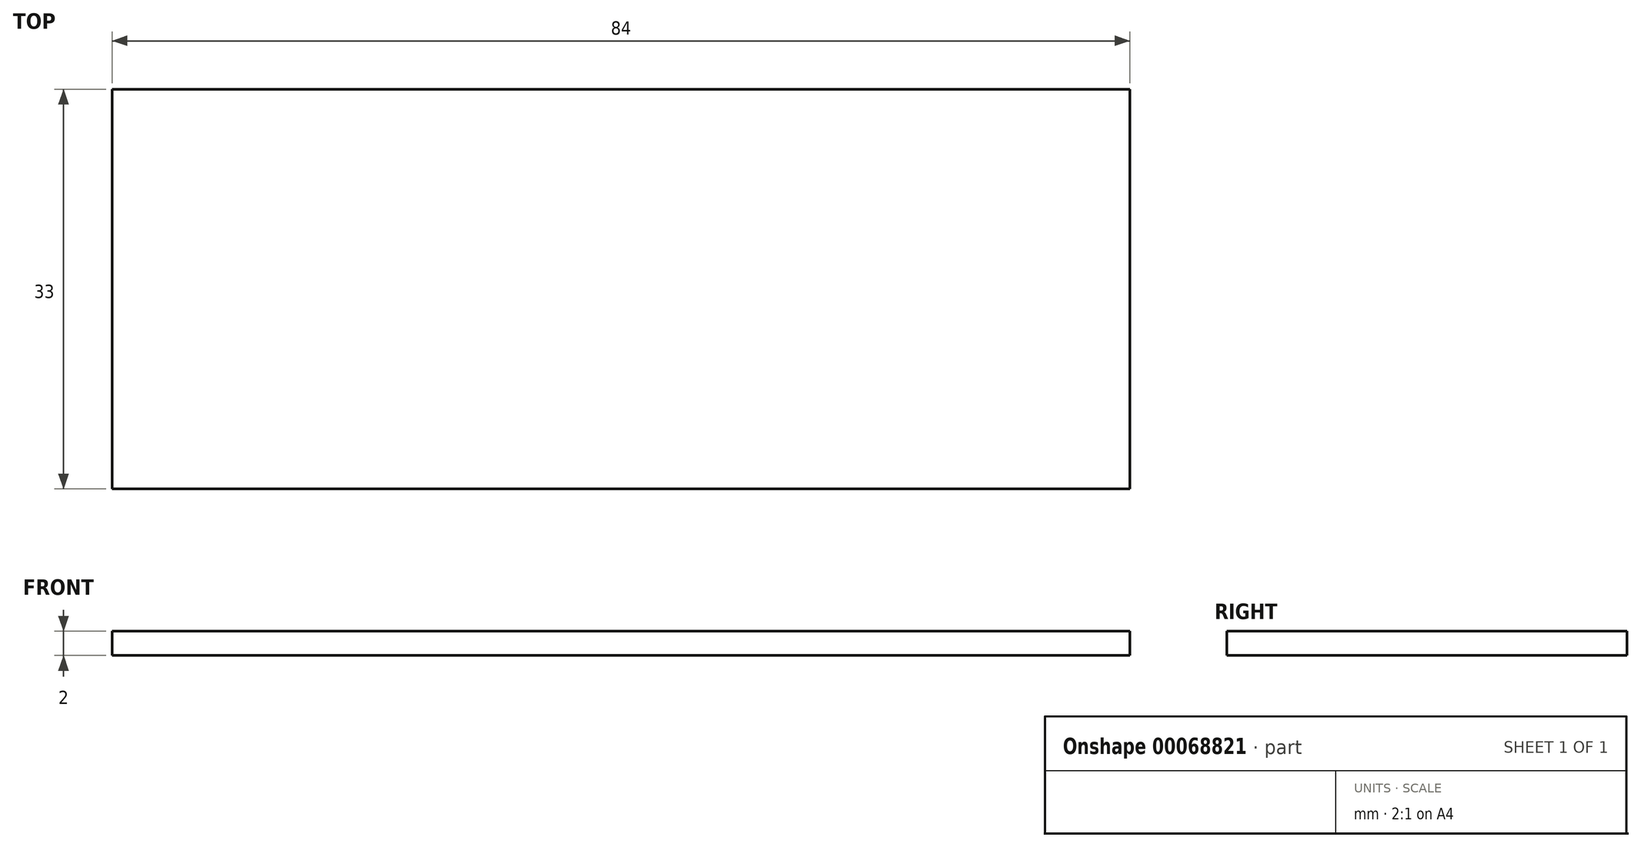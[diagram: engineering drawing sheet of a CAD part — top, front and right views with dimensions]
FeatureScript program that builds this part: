
annotation { "Feature Type Name" : "Feature", "Feature Type Description" : "" }
export const myFeature = defineFeature(function(context is Context, id is Id, definition is map)
    precondition{}
    {
        {
            var Q0;
            Q0=qCreatedBy(makeId("Top.planeOp"),FACE);
            var sketch = newSketch(context, id + "F0", { "sketchPlane" : qUnion([Q0])});
            skLineSegment(sketch, "E0.bottom", {"start": v(0, 0) * mm, "end": v(84, 0) * mm});
            skLineSegment(sketch, "E0.top", {"start": v(0, -33) * mm, "end": v(84, -33) * mm});
            skLineSegment(sketch, "E0.left", {"start": v(0, 0) * mm, "end": v(0, -33) * mm});
            skLineSegment(sketch, "E0.right", {"start": v(84, 0) * mm, "end": v(84, -33) * mm});
            skSolve(sketch);
        }
        {
            var Q0;
            Q0 = qSketchRegion(id + "F0", true);
            extrude(context, id + "F1", {"entities" : qUnion([Q0]), "depth" : 2 * mm});
        }
    });
